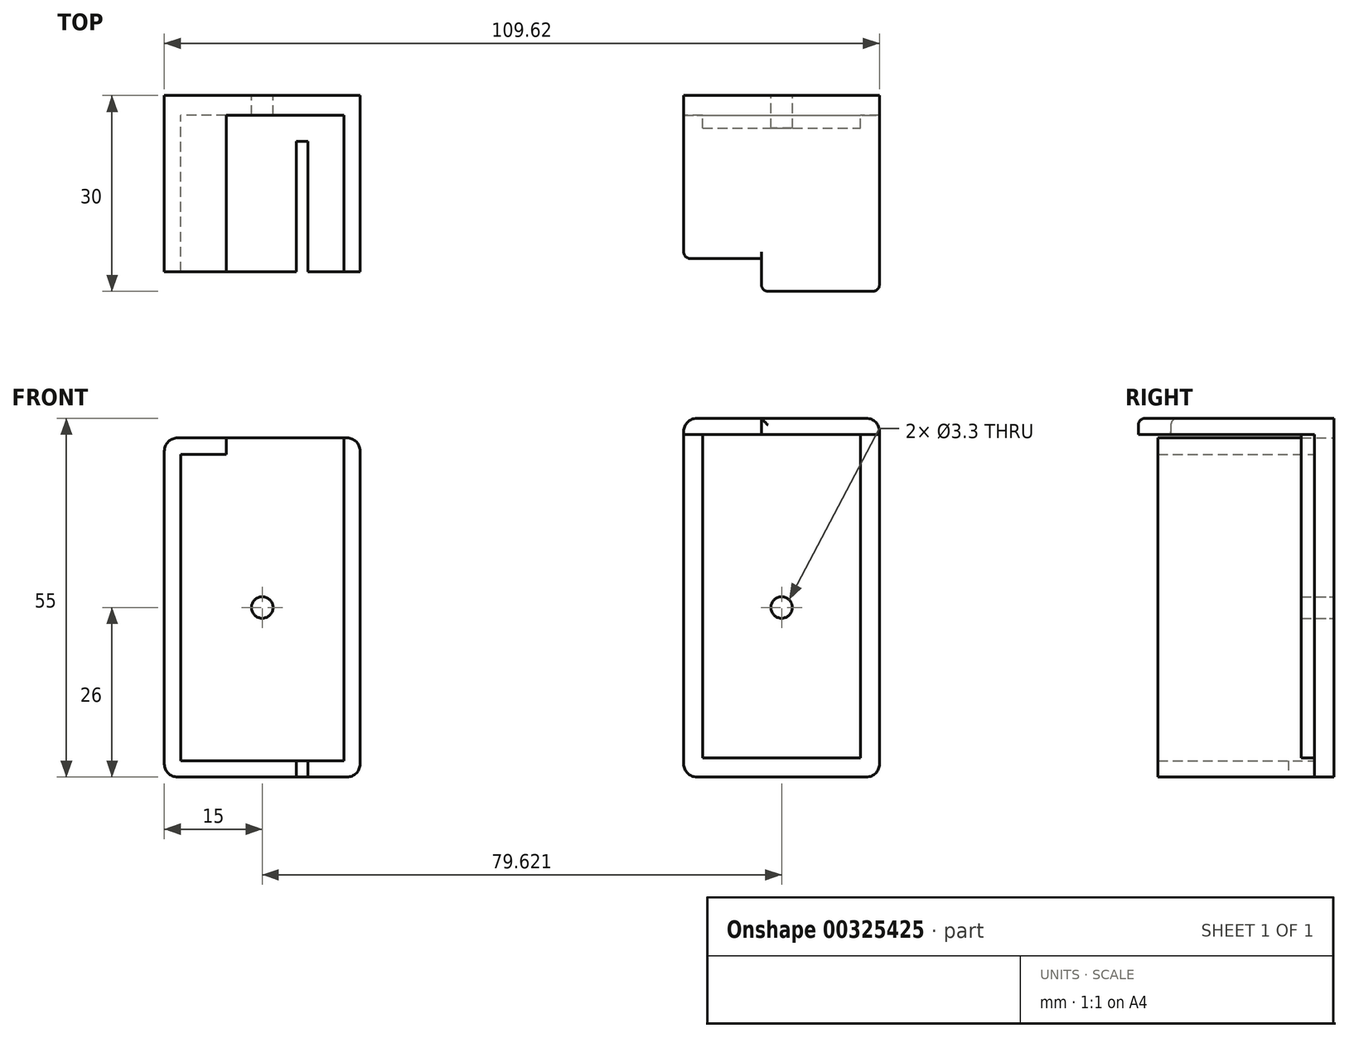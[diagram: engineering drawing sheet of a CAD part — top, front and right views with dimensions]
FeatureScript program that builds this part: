
annotation { "Feature Type Name" : "Feature", "Feature Type Description" : "" }
export const myFeature = defineFeature(function(context is Context, id is Id, definition is map)
    precondition{}
    {
        {
            var Q0;
            Q0=qCreatedBy(makeId("Front.planeOp"),FACE);
            var sketch = newSketch(context, id + "F0", { "sketchPlane" : qUnion([Q0])});
            skLineSegment(sketch, "E0.bottom", {"start": v(-2, 0) * mm, "end": v(-28, 0) * mm});
            skLineSegment(sketch, "E0.top", {"start": v(-2, 52) * mm, "end": v(-28, 52) * mm});
            skLineSegment(sketch, "E0.left", {"start": v(0, 2) * mm, "end": v(0, 50) * mm});
            skLineSegment(sketch, "E0.right", {"start": v(-30, 2) * mm, "end": v(-30, 50) * mm});
            skLineSegment(sketch, "E1.0", {"start": v(-2.5, 2.5) * mm, "end": v(-2.5, 49.5) * mm});
            skLineSegment(sketch, "E1.1", {"start": v(-2.5, 2.5) * mm, "end": v(-27.5, 2.5) * mm});
            skLineSegment(sketch, "E1.2", {"start": v(-27.5, 2.5) * mm, "end": v(-27.5, 49.5) * mm});
            skLineSegment(sketch, "E1.3", {"start": v(-2.5, 49.5) * mm, "end": v(-27.5, 49.5) * mm});
            skPoint(sketch, "E2.visualSharp", {"position": v(-30, 0) * mm});
            skArc(sketch, "E2.filletArc", {"start": v(-30, 2) * mm, "mid": v(-29.41, 0.59) * mm, "end": v(-28, 0) * mm});
            skPoint(sketch, "E3.visualSharp", {"position": v(0, 0) * mm});
            skArc(sketch, "E3.filletArc", {"start": v(-2, 0) * mm, "mid": v(-0.59, 0.59) * mm, "end": v(0, 2) * mm});
            skPoint(sketch, "E4.visualSharp", {"position": v(0, 52) * mm});
            skArc(sketch, "E4.filletArc", {"start": v(0, 50) * mm, "mid": v(-0.59, 51.41) * mm, "end": v(-2, 52) * mm});
            skPoint(sketch, "E5.visualSharp", {"position": v(-30, 52) * mm});
            skArc(sketch, "E5.filletArc", {"start": v(-28, 52) * mm, "mid": v(-29.41, 51.41) * mm, "end": v(-30, 50) * mm});
            skCircle(sketch, "E6", {"center": v(-15, 26) * mm, "radius": 1.65 * mm});
            skPoint(sketch, "E7.start.orphan", {"position": v(-15, 52) * mm});
            skPoint(sketch, "E8.trimOffspring.end.orphan", {"position": v(-15, 0) * mm});
            skSolve(sketch);
        }
        {
            var Q0;
            Q0=makeQuery(id+"F0.imprint","IMPRINT",FACE,{"disambiguationData":[TD([[makeQuery(id+"F0.imprint","IMPRINT",EDGE,{"derivedFrom":sQuery(id+"F0.wireOp",EDGE,"E0.bottom")}),-1.0]])]});
            extrude(context, id + "F1", {"entities" : qUnion([Q0]), "depth" : 27 * mm});
        }
        {
            var Q0;
            Q0=makeQuery(id+"F0.imprint","IMPRINT",FACE,{"disambiguationData":[TD([[makeQuery(id+"F0.imprint","IMPRINT",EDGE,{"derivedFrom":sQuery(id+"F0.wireOp",EDGE,"E1.0")}),1.0]])]});
            extrude(context, id + "F2", {"entities" : qUnion([Q0]), "operationType" : NewBodyOperationType.ADD, "depth" : 3 * mm});
        }
        {
            var Q0;
            Q0=makeQuery(id+"F1.opExtrude","SWEPT_FACE",FACE,{"disambiguationData":[OSD([sQuery(id+"F0.wireOp",EDGE,"E0.bottom")])]});
            var sketch = newSketch(context, id + "F3", { "sketchPlane" : qUnion([Q0])});
            skPoint(sketch, "E9", {"position": v(-8, 27) * mm});
            skPoint(sketch, "E10", {"position": v(-9.8, 27) * mm});
            skLineSegment(sketch, "E11", {"start": v(-9.8, 27) * mm, "end": v(-9.8, 7) * mm});
            skLineSegment(sketch, "E12", {"start": v(-8, 27) * mm, "end": v(-8, 7) * mm});
            skLineSegment(sketch, "E13", {"start": v(-8, 7) * mm, "end": v(-9.8, 7) * mm});
            skSolve(sketch);
        }
        {
            var Q0;
            {var subQ0=sQuery(id+"F3.wireOp",EDGE,"E11");Q0=makeQuery(id+"F3.imprint","IMPRINT",FACE,{"disambiguationData":[TD([[makeQuery(id+"F3.imprint","IMPRINT",EDGE,{"derivedFrom":subQ0}),1.0]])]});}
            extrude(context, id + "F4", {"entities" : qUnion([Q0]), "operationType" : NewBodyOperationType.REMOVE, "oppositeDirection" : true, "depth" : 25 * mm});
        }
        {
            var Q0;
            Q0=makeQuery(id+"F1.opExtrude","SWEPT_FACE",FACE,{"disambiguationData":[OSD([sQuery(id+"F0.wireOp",EDGE,"E0.top")])]});
            var sketch = newSketch(context, id + "F5", { "sketchPlane" : qUnion([Q0])});
            skPoint(sketch, "E14", {"position": v(-2.5, -27) * mm});
            skLineSegment(sketch, "E15", {"start": v(-2.5, -27) * mm, "end": v(-2.5, -3) * mm});
            skLineSegment(sketch, "E16", {"start": v(-2.5, -3) * mm, "end": v(-20.5, -3) * mm});
            skLineSegment(sketch, "E17", {"start": v(-20.5, -3) * mm, "end": v(-20.5, -27) * mm});
            skSolve(sketch);
        }
        {
            var Q0;
            {var subQ0=sQuery(id+"F5.wireOp",EDGE,"E15");Q0=makeQuery(id+"F5.imprint","IMPRINT",FACE,{"disambiguationData":[TD([[makeQuery(id+"F5.imprint","IMPRINT",EDGE,{"derivedFrom":subQ0}),1.0]])]});}
            extrude(context, id + "F6", {"entities" : qUnion([Q0]), "operationType" : NewBodyOperationType.REMOVE, "oppositeDirection" : true, "depth" : 25 * mm});
        }
        {
            var Q0;
            Q0=qCreatedBy(makeId("Front.planeOp"),FACE);
            var sketch = newSketch(context, id + "F7", { "sketchPlane" : qUnion([Q0])});
            skLineSegment(sketch, "E18.bottom", {"start": v(51.62, 0) * mm, "end": v(77.62, 0) * mm});
            skLineSegment(sketch, "E18.left", {"start": v(49.62, 2) * mm, "end": v(49.62, 50) * mm});
            skLineSegment(sketch, "E18.right", {"start": v(79.62, 2) * mm, "end": v(79.62, 50) * mm});
            skPoint(sketch, "E19.visualSharp", {"position": v(49.62, 52) * mm});
            skPoint(sketch, "E20.visualSharp", {"position": v(79.62, 52) * mm});
            skPoint(sketch, "E21.visualSharp", {"position": v(79.62, 0) * mm});
            skArc(sketch, "E21.filletArc", {"start": v(77.62, 0) * mm, "mid": v(79.04, 0.59) * mm, "end": v(79.62, 2) * mm});
            skPoint(sketch, "E22.visualSharp", {"position": v(49.62, 0) * mm});
            skArc(sketch, "E22.filletArc", {"start": v(49.62, 2) * mm, "mid": v(50.2, 0.59) * mm, "end": v(51.62, 0) * mm});
            skLineSegment(sketch, "E23.0", {"start": v(52.52, 2.9) * mm, "end": v(52.52, 49.1) * mm});
            skLineSegment(sketch, "E23.1", {"start": v(52.52, 2.9) * mm, "end": v(76.72, 2.9) * mm});
            skLineSegment(sketch, "E23.2", {"start": v(76.72, 2.9) * mm, "end": v(76.72, 49.1) * mm});
            skCircle(sketch, "E24", {"center": v(64.62, 26) * mm, "radius": 1.65 * mm});
            skPoint(sketch, "E25.start.orphan", {"position": v(64.62, 52) * mm});
            skPoint(sketch, "E26.trimOffspring.end.orphan", {"position": v(64.62, 0) * mm});
            skPoint(sketch, "E27", {"position": v(69.12, 49.1) * mm});
            skLineSegment(sketch, "E28", {"start": v(52.52, 49.1) * mm, "end": v(52.52, 52) * mm});
            skLineSegment(sketch, "E29", {"start": v(49.62, 52) * mm, "end": v(49.62, 53) * mm});
            skLineSegment(sketch, "E30", {"start": v(79.62, 50) * mm, "end": v(79.62, 52) * mm});
            skLineSegment(sketch, "E31", {"start": v(79.62, 52) * mm, "end": v(79.62, 53) * mm});
            skLineSegment(sketch, "E32", {"start": v(77.62, 55) * mm, "end": v(51.62, 55) * mm});
            skLineSegment(sketch, "E33", {"start": v(49.62, 50) * mm, "end": v(49.62, 52) * mm});
            skPoint(sketch, "E34", {"position": v(79.62, 52.5) * mm});
            skLineSegment(sketch, "E35", {"start": v(76.72, 52.5) * mm, "end": v(52.52, 52.5) * mm});
            skLineSegment(sketch, "E36", {"start": v(52.52, 52) * mm, "end": v(52.52, 52.5) * mm});
            skLineSegment(sketch, "E37", {"start": v(76.72, 49.1) * mm, "end": v(76.72, 52.5) * mm});
            skPoint(sketch, "E38.visualSharp", {"position": v(49.62, 55) * mm});
            skArc(sketch, "E38.filletArc", {"start": v(51.62, 55) * mm, "mid": v(50.2, 54.41) * mm, "end": v(49.62, 53) * mm});
            skPoint(sketch, "E39.visualSharp", {"position": v(79.62, 55) * mm});
            skArc(sketch, "E39.filletArc", {"start": v(79.62, 53) * mm, "mid": v(79.04, 54.41) * mm, "end": v(77.62, 55) * mm});
            skPoint(sketch, "E18.top.start.orphan", {"position": v(51.62, 52) * mm});
            skPoint(sketch, "E40.trimOffspring.end.orphan", {"position": v(77.62, 52) * mm});
            skLineSegment(sketch, "E41", {"start": v(79.62, 52.5) * mm, "end": v(76.72, 52.5) * mm});
            skLineSegment(sketch, "E42", {"start": v(52.52, 52.5) * mm, "end": v(49.62, 52.5) * mm});
            skLineSegment(sketch, "E43", {"start": v(52.52, 52.5) * mm, "end": v(52.52, 55) * mm});
            skPoint(sketch, "E44", {"position": v(61.52, 55) * mm});
            skLineSegment(sketch, "E45", {"start": v(61.52, 55) * mm, "end": v(61.52, 52.5) * mm});
            skSolve(sketch);
        }
        {
            var Q0;
            Q0=makeQuery(id+"F7.imprint","IMPRINT",FACE,{"disambiguationData":[TD([[makeQuery(id+"F7.imprint","IMPRINT",EDGE,{"derivedFrom":sQuery(id+"F7.wireOp",EDGE,"E18.bottom")}),1.0]])]});
            extrude(context, id + "F8", {"entities" : qUnion([Q0]), "depth" : 3 * mm});
        }
        {
            var Q0;
            Q0=makeQuery(id+"F7.imprint","IMPRINT",FACE,{"disambiguationData":[TD([[makeQuery(id+"F7.imprint","IMPRINT",EDGE,{"derivedFrom":sQuery(id+"F7.wireOp",EDGE,"E23.0")}),-1.0]])]});
            extrude(context, id + "F9", {"entities" : qUnion([Q0]), "operationType" : NewBodyOperationType.ADD, "depth" : 5 * mm});
        }
        {
            var Q0;
            {var subQ0=sQuery(id+"F7.wireOp",EDGE,"E39.filletArc");Q0=makeQuery(id+"F7.imprint","IMPRINT",FACE,{"disambiguationData":[TD([[makeQuery(id+"F7.imprint","IMPRINT",EDGE,{"derivedFrom":subQ0}),1.0]])]});}
            extrude(context, id + "F10", {"entities" : qUnion([Q0]), "operationType" : NewBodyOperationType.ADD, "depth" : 30 * mm});
        }
        {
            var Q0;
            {var subQ0=sQuery(id+"F7.wireOp",EDGE,"E43");Q0=makeQuery(id+"F7.imprint","IMPRINT",FACE,{"disambiguationData":[TD([[makeQuery(id+"F7.imprint","IMPRINT",EDGE,{"derivedFrom":subQ0}),-1.0]])]});}
            var Q1;
            {var subQ0=sQuery(id+"F7.wireOp",EDGE,"E38.filletArc");Q1=makeQuery(id+"F7.imprint","IMPRINT",FACE,{"disambiguationData":[TD([[makeQuery(id+"F7.imprint","IMPRINT",EDGE,{"derivedFrom":subQ0}),1.0]])]});}
            extrude(context, id + "F11", {"entities" : qUnion([Q0, Q1]), "operationType" : NewBodyOperationType.ADD, "depth" : 25 * mm});
        }
        {
            var Q0;
            Q0=makeQuery(id+"F11.opExtrude","CAP_EDGE",EDGE,{"disambiguationData":[OSD([sQuery(id+"F7.wireOp",EDGE,"E45")])],"isStart":false});
            var Q1;
            Q1=makeQuery(id+"F10.opExtrude","CAP_EDGE",EDGE,{"disambiguationData":[OSD([sQuery(id+"F7.wireOp",EDGE,"E45")])],"isStart":false});
            var Q2;
            Q2=makeQuery(id+"F11.opExtrude","CAP_EDGE",EDGE,{"disambiguationData":[OSD([sQuery(id+"F7.wireOp",EDGE,"E38.filletArc")])],"isStart":false});
            var Q3;
            Q3=makeQuery(id+"F10.opExtrude","CAP_EDGE",EDGE,{"disambiguationData":[OSD([sQuery(id+"F7.wireOp",EDGE,"E39.filletArc")])],"isStart":false});
            fillet(context, id + "F12", {"entities" : qUnion([Q0, Q1, Q2, Q3]), "radius" : 1 * mm, "tangentPropagation" : true, "allowEdgeOverflow" : false});
        }
    });
